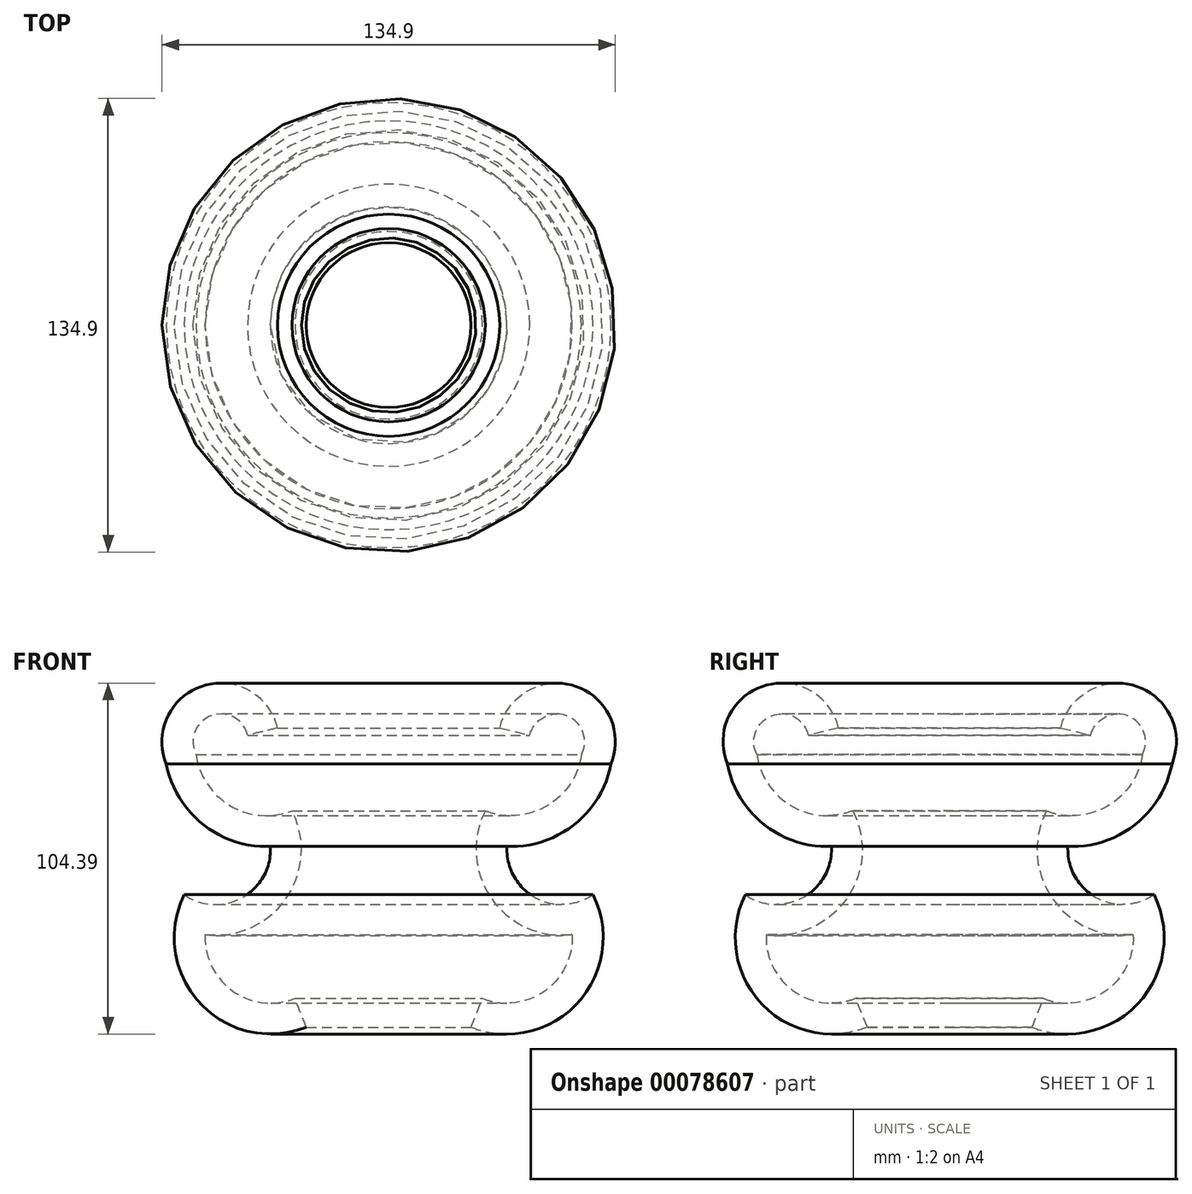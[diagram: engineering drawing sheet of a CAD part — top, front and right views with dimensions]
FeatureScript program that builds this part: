
annotation { "Feature Type Name" : "Feature", "Feature Type Description" : "" }
export const myFeature = defineFeature(function(context is Context, id is Id, definition is map)
    precondition{}
    {
        {
            var Q0;
            Q0=qCreatedBy(makeId("Front.planeOp"),FACE);
            var sketch = newSketch(context, id + "F0", { "sketchPlane" : qUnion([Q0])});
            skArc(sketch, "E0", {"start": v(-60.83, 0) * mm, "mid": v(-56.21, -32.18) * mm, "end": v(-24.5, -39.38) * mm});
            skArc(sketch, "E1", {"start": v(-60.83, 0) * mm, "mid": v(-43.53, -0.8) * mm, "end": v(-35.19, 14.39) * mm});
            skArc(sketch, "E2", {"start": v(-66.17, 38.96) * mm, "mid": v(-55.24, 20.92) * mm, "end": v(-35.19, 14.39) * mm});
            skArc(sketch, "E3", {"start": v(-33.05, 49.64) * mm, "mid": v(-55.36, 62.12) * mm, "end": v(-66.17, 38.96) * mm});
            skArc(sketch, "E4.0", {"start": v(-41.98, 47.47) * mm, "mid": v(-52.93, 53.24) * mm, "end": v(-57.3, 41.67) * mm});
            skArc(sketch, "E4.1", {"start": v(-57.3, 41.67) * mm, "mid": v(-47.05, 26.42) * mm, "end": v(-28.72, 25.01) * mm});
            skArc(sketch, "E4.2", {"start": v(-54.6, -11.9) * mm, "mid": v(-30.61, -1.2) * mm, "end": v(-28.72, 25.01) * mm});
            skArc(sketch, "E4.3", {"start": v(-54.6, -11.9) * mm, "mid": v(-46.41, -28.63) * mm, "end": v(-27.91, -30.84) * mm});
            skLineSegment(sketch, "E5", {"start": v(-41.98, 47.47) * mm, "end": v(-33.05, 49.64) * mm});
            skLineSegment(sketch, "E6", {"start": v(-27.91, -30.84) * mm, "end": v(-24.5, -39.38) * mm});
            skLineSegment(sketch, "E7", {"start": v(0, -53.62) * mm, "end": v(0, 84.12) * mm, "construction": true});
            skSolve(sketch);
        }
        {
            var Q0;
            Q0=makeQuery(id+"F0.imprint","IMPRINT",FACE,{"disambiguationData":[TD([[makeQuery(id+"F0.imprint","IMPRINT",EDGE,{"derivedFrom":sQuery(id+"F0.wireOp",EDGE,"E0")}),1.0]])]});
            var Q1;
            Q1=sQuery(id+"F0.wireOp",EDGE,"E7");
            revolve(context, id + "F1", {"entities" : qUnion([Q0]), "axis" : qUnion([Q1]), "revolveType" : RevolveType.FULL});
        }
    });
